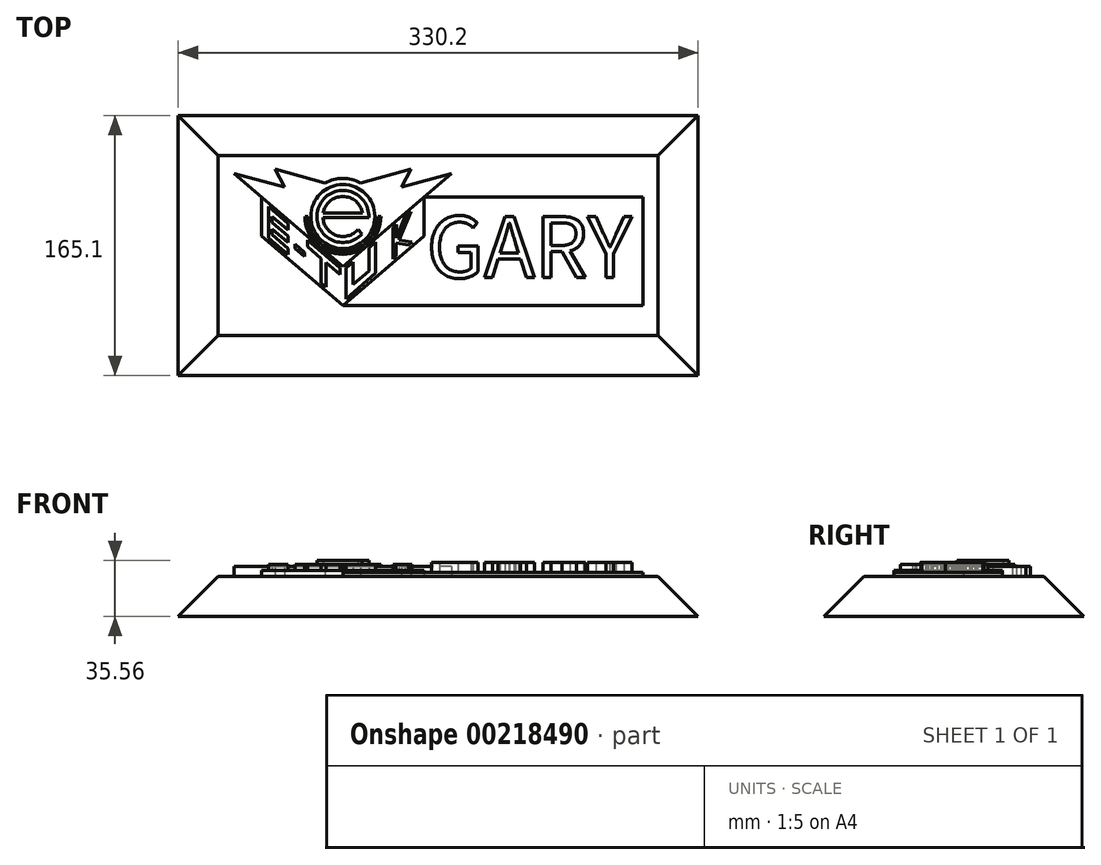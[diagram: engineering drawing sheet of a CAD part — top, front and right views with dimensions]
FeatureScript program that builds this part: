
annotation { "Feature Type Name" : "Feature", "Feature Type Description" : "" }
export const myFeature = defineFeature(function(context is Context, id is Id, definition is map)
    precondition{}
    {
        {
            var Q0;
            Q0=qCreatedBy(makeId("Top.planeOp"),FACE);
            var sketch = newSketch(context, id + "F0", { "sketchPlane" : qUnion([Q0])});
            skArc(sketch, "E0", {"start": v(12.53, 2.07) * mm, "mid": v(0, 12.7) * mm, "end": v(-12.53, 2.07) * mm});
            skArc(sketch, "E1", {"start": v(16.5, -0.78) * mm, "mid": v(-15.23, 6.37) * mm, "end": v(12.14, -11.18) * mm});
            skLineSegment(sketch, "E2", {"start": v(12.7, -0.78) * mm, "end": v(-12.68, -0.78) * mm});
            skLineSegment(sketch, "E3", {"start": v(-12.68, -0.78) * mm, "end": v(16.5, -0.78) * mm});
            skLineSegment(sketch, "E4", {"start": v(9.59, -8.33) * mm, "end": v(12.14, -11.18) * mm});
            skArc(sketch, "E5.trimOffspring", {"start": v(-12.68, -0.78) * mm, "mid": v(-4.08, -12.03) * mm, "end": v(9.59, -8.33) * mm});
            skLineSegment(sketch, "E6", {"start": v(-12.53, 2.07) * mm, "end": v(12.53, 2.07) * mm});
            skSolve(sketch);
        }
        {
            var Q0;
            Q0=makeQuery(id+"F0.imprint","IMPRINT",FACE,{"disambiguationData":[TD([[makeQuery(id+"F0.imprint","IMPRINT",EDGE,{"derivedFrom":sQuery(id+"F0.wireOp",EDGE,"E0")}),-1.0]])]});
            extrude(context, id + "F1", {"entities" : qUnion([Q0]), "depth" : 10.16 * mm});
        }
        {
            var Q0;
            Q0=qCreatedBy(makeId("Top.planeOp"),FACE);
            var sketch = newSketch(context, id + "F2", { "sketchPlane" : qUnion([Q0])});
            skCircle(sketch, "E7", {"center": v(0, 0) * mm, "radius": 20.32 * mm});
            skSolve(sketch);
        }
        {
            var Q0;
            Q0=qSketchRegion(id+"F2",true);
            extrude(context, id + "F3", {"entities" : qUnion([Q0]), "operationType" : NewBodyOperationType.ADD, "depth" : 7.62 * mm});
        }
        {
            var Q0;
            Q0=qCreatedBy(makeId("Top.planeOp"),FACE);
            var sketch = newSketch(context, id + "F4", { "sketchPlane" : qUnion([Q0])});
            skLineSegment(sketch, "E8", {"start": v(-69.02, 27.27) * mm, "end": v(-37.13, 18.72) * mm});
            skLineSegment(sketch, "E9", {"start": v(-37.13, 18.72) * mm, "end": v(-43.14, 30.14) * mm});
            skLineSegment(sketch, "E10", {"start": v(-43.14, 30.14) * mm, "end": v(-11.32, 21.31) * mm});
            skLineSegment(sketch, "E11", {"start": v(-69.02, 27.27) * mm, "end": v(0, -31.75) * mm});
            skLineSegment(sketch, "E12.MirrorCS", {"start": v(43.14, 30.14) * mm, "end": v(11.32, 21.31) * mm});
            skLineSegment(sketch, "E13.MirrorCS", {"start": v(69.02, 27.27) * mm, "end": v(0, -31.75) * mm});
            skLineSegment(sketch, "E14.MirrorCS", {"start": v(69.02, 27.27) * mm, "end": v(37.13, 18.72) * mm});
            skLineSegment(sketch, "E15.MirrorCS", {"start": v(37.13, 18.72) * mm, "end": v(43.14, 30.14) * mm});
            skArc(sketch, "E16.trimOffspring", {"start": v(11.32, 21.31) * mm, "mid": v(0, 24.13) * mm, "end": v(-11.32, 21.31) * mm});
            skSolve(sketch);
        }
        {
            var Q0;
            Q0=qSketchRegion(id+"F4",true);
            var Q1;
            Q1=makeQuery(id+"F2.imprint","IMPRINT",FACE,{"disambiguationData":[TD([[makeQuery(id+"F2.imprint","IMPRINT",EDGE,{"derivedFrom":sQuery(id+"F2.wireOp",EDGE,"E7")}),1.0]])]});
            extrude(context, id + "F5", {"entities" : qUnion([Q0, Q1]), "operationType" : NewBodyOperationType.ADD, "depth" : 6.35 * mm});
        }
        {
            var Q0;
            Q0=qCreatedBy(makeId("Top.planeOp"),FACE);
            var sketch = newSketch(context, id + "F6", { "sketchPlane" : qUnion([Q0])});
            skLineSegment(sketch, "E17", {"start": v(-51.6, -12.38) * mm, "end": v(0, -56.51) * mm});
            skLineSegment(sketch, "E18", {"start": v(0, -56.51) * mm, "end": v(51.6, -12.38) * mm});
            skLineSegment(sketch, "E19", {"start": v(-51.6, 12.38) * mm, "end": v(-51.6, -12.38) * mm});
            skLineSegment(sketch, "E20", {"start": v(51.6, 12.38) * mm, "end": v(51.6, -12.38) * mm});
            skLineSegment(sketch, "E21", {"start": v(-51.6, 12.38) * mm, "end": v(0, -31.75) * mm});
            skLineSegment(sketch, "E22", {"start": v(0, -31.75) * mm, "end": v(51.6, 12.38) * mm});
            skSolve(sketch);
        }
        {
            var Q0;
            Q0=qSketchRegion(id+"F6",true);
            extrude(context, id + "F7", {"entities" : qUnion([Q0]), "operationType" : NewBodyOperationType.ADD, "depth" : 3.8 * mm});
        }
        {
            var Q0;
            Q0=makeQuery(id+"F7.opExtrude","CAP_FACE",FACE,{"disambiguationData":[OSD([sQuery(id+"F6.wireOp",EDGE,"E17"),sQuery(id+"F6.wireOp",EDGE,"E18"),sQuery(id+"F6.wireOp",EDGE,"E19"),sQuery(id+"F6.wireOp",EDGE,"E20"),sQuery(id+"F6.wireOp",EDGE,"E21"),sQuery(id+"F6.wireOp",EDGE,"E22")])],"isStart":false});
            var sketch = newSketch(context, id + "F8", { "sketchPlane" : qUnion([Q0])});
            skPoint(sketch, "E23.startSnap0", {"position": v(-51.6, 0) * mm});
            skLineSegment(sketch, "E24", {"start": v(-51.6, -9.87) * mm, "end": v(-51.6, 9.87) * mm, "construction": true});
            skLineSegment(sketch, "E25", {"start": v(-47.26, 6.16) * mm, "end": v(-34.74, -4.55) * mm});
            skLineSegment(sketch, "E26", {"start": v(-34.74, -4.55) * mm, "end": v(-34.74, -8.63) * mm});
            skLineSegment(sketch, "E27", {"start": v(-34.74, -8.63) * mm, "end": v(-44.83, 0) * mm});
            skLineSegment(sketch, "E28", {"start": v(-44.83, 0) * mm, "end": v(-44.83, -3.75) * mm});
            skLineSegment(sketch, "E29", {"start": v(-44.83, -3.75) * mm, "end": v(-34.74, -12.38) * mm});
            skLineSegment(sketch, "E30", {"start": v(-34.74, -12.38) * mm, "end": v(-34.74, -16.46) * mm});
            skLineSegment(sketch, "E31", {"start": v(-34.74, -16.46) * mm, "end": v(-44.83, -7.83) * mm});
            skLineSegment(sketch, "E32", {"start": v(-44.83, -7.83) * mm, "end": v(-44.83, -11.58) * mm});
            skLineSegment(sketch, "E33", {"start": v(-44.83, -11.58) * mm, "end": v(-34.74, -20.21) * mm});
            skLineSegment(sketch, "E34", {"start": v(-34.74, -20.21) * mm, "end": v(-34.74, -24.3) * mm});
            skLineSegment(sketch, "E35", {"start": v(-34.74, -24.3) * mm, "end": v(-47.26, -13.59) * mm});
            skLineSegment(sketch, "E36", {"start": v(-47.26, 6.16) * mm, "end": v(-47.26, -13.59) * mm});
            skLineSegment(sketch, "E37", {"start": v(-30.38, -20.21) * mm, "end": v(-30.38, -17.65) * mm});
            skLineSegment(sketch, "E38", {"start": v(-30.38, -17.65) * mm, "end": v(-24.17, -22.96) * mm});
            skLineSegment(sketch, "E39", {"start": v(-24.17, -22.96) * mm, "end": v(-24.17, -25.53) * mm});
            skLineSegment(sketch, "E40", {"start": v(-24.17, -25.53) * mm, "end": v(-30.38, -20.21) * mm});
            skLineSegment(sketch, "E41", {"start": v(-22.38, -15.12) * mm, "end": v(-1.9, -32.63) * mm});
            skLineSegment(sketch, "E42", {"start": v(-1.9, -32.63) * mm, "end": v(-1.9, -36.71) * mm});
            skLineSegment(sketch, "E43", {"start": v(-1.9, -36.71) * mm, "end": v(-10.6, -29.28) * mm});
            skLineSegment(sketch, "E44", {"start": v(-10.6, -29.28) * mm, "end": v(-10.6, -44.95) * mm});
            skLineSegment(sketch, "E45", {"start": v(-10.6, -44.95) * mm, "end": v(-13.7, -42.3) * mm});
            skLineSegment(sketch, "E46", {"start": v(-13.7, -42.3) * mm, "end": v(-13.7, -26.63) * mm});
            skLineSegment(sketch, "E47", {"start": v(-13.7, -26.63) * mm, "end": v(-22.38, -19.2) * mm});
            skLineSegment(sketch, "E48", {"start": v(-22.38, -19.2) * mm, "end": v(-22.38, -15.12) * mm});
            skLineSegment(sketch, "E49", {"start": v(1.9, -32.62) * mm, "end": v(6.3, -28.86) * mm});
            skLineSegment(sketch, "E50", {"start": v(6.3, -28.86) * mm, "end": v(6.3, -43.26) * mm});
            skLineSegment(sketch, "E51", {"start": v(6.3, -43.26) * mm, "end": v(16.5, -34.54) * mm});
            skLineSegment(sketch, "E52", {"start": v(16.5, -34.54) * mm, "end": v(16.5, -20.14) * mm});
            skLineSegment(sketch, "E53", {"start": v(16.5, -20.14) * mm, "end": v(20.85, -16.3) * mm});
            skLineSegment(sketch, "E54", {"start": v(20.85, -16.3) * mm, "end": v(20.85, -36.06) * mm});
            skLineSegment(sketch, "E55", {"start": v(20.85, -36.06) * mm, "end": v(1.9, -52.37) * mm});
            skLineSegment(sketch, "E56", {"start": v(1.9, -52.37) * mm, "end": v(1.9, -32.62) * mm});
            skLineSegment(sketch, "E57", {"start": v(31.73, -7.12) * mm, "end": v(31.73, -27.15) * mm});
            skLineSegment(sketch, "E58", {"start": v(31.73, -27.15) * mm, "end": v(33.91, -25.22) * mm});
            skLineSegment(sketch, "E59", {"start": v(33.91, -25.22) * mm, "end": v(33.91, -16.82) * mm});
            skLineSegment(sketch, "E60", {"start": v(33.94, -13.64) * mm, "end": v(33.94, -5.23) * mm});
            skLineSegment(sketch, "E61", {"start": v(33.94, -5.23) * mm, "end": v(31.73, -7.12) * mm});
            skLineSegment(sketch, "E62", {"start": v(41.79, -18.27) * mm, "end": v(44, -16.38) * mm});
            skLineSegment(sketch, "E63", {"start": v(33.94, -13.64) * mm, "end": v(39.5, 0) * mm});
            skLineSegment(sketch, "E64", {"start": v(33.91, -16.82) * mm, "end": v(41.79, -18.27) * mm});
            skLineSegment(sketch, "E65", {"start": v(44, -16.38) * mm, "end": v(35.85, -14.87) * mm});
            skLineSegment(sketch, "E66", {"start": v(35.85, -14.87) * mm, "end": v(43.2, 3.16) * mm});
            skLineSegment(sketch, "E67", {"start": v(39.5, 0) * mm, "end": v(43.2, 3.16) * mm});
            skSolve(sketch);
        }
        {
            var Q0;
            Q0=qSketchRegion(id+"F8",true);
            extrude(context, id + "F9", {"entities" : qUnion([Q0]), "operationType" : NewBodyOperationType.ADD, "depth" : 3.8 * mm});
        }
        {
            var Q0;
            Q0=makeQuery(id+"F5.boolean.opBoolean","MERGE",FACE,{"derivedFrom":[makeQuery(id+"F5.opExtrude","CAP_FACE",FACE,{"disambiguationData":[OSD([sQuery(id+"F2.wireOp",EDGE,"E7")])],"isStart":false}),makeQuery(id+"F5.opExtrude","CAP_FACE",FACE,{"disambiguationData":[OSD([sQuery(id+"F4.wireOp",EDGE,"E8"),sQuery(id+"F4.wireOp",EDGE,"E9"),sQuery(id+"F4.wireOp",EDGE,"E10"),sQuery(id+"F4.wireOp",EDGE,"E11"),sQuery(id+"F4.wireOp",EDGE,"E13.MirrorCS"),sQuery(id+"F4.wireOp",EDGE,"E14.MirrorCS"),sQuery(id+"F4.wireOp",EDGE,"E12.MirrorCS"),sQuery(id+"F4.wireOp",EDGE,"E15.MirrorCS"),sQuery(id+"F4.wireOp",EDGE,"E16.trimOffspring")])],"isStart":false})]});
            var sketch = newSketch(context, id + "F10", { "sketchPlane" : qUnion([Q0])});
            skArc(sketch, "E68", {"start": v(-24.13, 0) * mm, "mid": v(0, -24.13) * mm, "end": v(24.13, 0) * mm});
            skArc(sketch, "E69", {"start": v(-22.23, 0) * mm, "mid": v(0, -22.23) * mm, "end": v(22.23, 0) * mm});
            skLineSegment(sketch, "E70", {"start": v(-24.13, 0) * mm, "end": v(-22.23, 0) * mm});
            skLineSegment(sketch, "E71", {"start": v(24.13, 0) * mm, "end": v(22.23, 0) * mm});
            skSolve(sketch);
        }
        {
            var Q0;
            Q0=qSketchRegion(id+"F10",true);
            extrude(context, id + "F11", {"entities" : qUnion([Q0]), "operationType" : NewBodyOperationType.ADD, "depth" : 1.27 * mm});
        }
        {
            var Q0;
            {var subQ0=sQuery(id+"F2.wireOp",EDGE,"E7");Q0=makeQuery(id+"F7.boolean.opBoolean","MERGE",FACE,{"derivedFrom":[makeQuery(id+"F5.boolean.opBoolean","MERGE",FACE,{"derivedFrom":[makeQuery(id+"F3.boolean.opBoolean","MERGE",FACE,{"derivedFrom":[makeQuery(id+"F1.opExtrude","CAP_FACE",FACE,{"disambiguationData":[OSD([sQuery(id+"F0.wireOp",EDGE,"E0"),sQuery(id+"F0.wireOp",EDGE,"E1"),sQuery(id+"F0.wireOp",EDGE,"E3"),sQuery(id+"F0.wireOp",EDGE,"E4"),sQuery(id+"F0.wireOp",EDGE,"E5.trimOffspring"),sQuery(id+"F0.wireOp",EDGE,"E6")])],"isStart":true}),makeQuery(id+"F3.opExtrude","CAP_FACE",FACE,{"disambiguationData":[OSD([subQ0])],"isStart":true})]}),makeQuery(id+"F5.opExtrude","CAP_FACE",FACE,{"disambiguationData":[OSD([subQ0])],"isStart":true}),makeQuery(id+"F5.opExtrude","CAP_FACE",FACE,{"disambiguationData":[OSD([sQuery(id+"F4.wireOp",EDGE,"E8"),sQuery(id+"F4.wireOp",EDGE,"E9"),sQuery(id+"F4.wireOp",EDGE,"E10"),sQuery(id+"F4.wireOp",EDGE,"E11"),sQuery(id+"F4.wireOp",EDGE,"E13.MirrorCS"),sQuery(id+"F4.wireOp",EDGE,"E14.MirrorCS"),sQuery(id+"F4.wireOp",EDGE,"E12.MirrorCS"),sQuery(id+"F4.wireOp",EDGE,"E15.MirrorCS"),sQuery(id+"F4.wireOp",EDGE,"E16.trimOffspring")])],"isStart":true})]}),makeQuery(id+"F7.opExtrude","CAP_FACE",FACE,{"disambiguationData":[OSD([sQuery(id+"F6.wireOp",EDGE,"E17"),sQuery(id+"F6.wireOp",EDGE,"E18"),sQuery(id+"F6.wireOp",EDGE,"E19"),sQuery(id+"F6.wireOp",EDGE,"E20"),sQuery(id+"F6.wireOp",EDGE,"E21"),sQuery(id+"F6.wireOp",EDGE,"E22")])],"isStart":true})]});}
            var sketch = newSketch(context, id + "F12", { "sketchPlane" : qUnion([Q0])});
            skLineSegment(sketch, "E72.bottom", {"start": v(0, 56.51) * mm, "end": v(190.5, 56.51) * mm});
            skLineSegment(sketch, "E72.right", {"start": v(190.5, 56.51) * mm, "end": v(190.5, -12.38) * mm});
            skLineSegment(sketch, "E73", {"start": v(51.6, -12.38) * mm, "end": v(190.5, -12.38) * mm});
            skLineSegment(sketch, "E74", {"start": v(0, 56.51) * mm, "end": v(51.6, 12.38) * mm});
            skLineSegment(sketch, "E75", {"start": v(51.6, 12.38) * mm, "end": v(51.6, -12.38) * mm});
            skSolve(sketch);
        }
        {
            var Q0;
            Q0=qSketchRegion(id+"F12",true);
            extrude(context, id + "F13", {"entities" : qUnion([Q0]), "operationType" : NewBodyOperationType.ADD, "oppositeDirection" : true, "depth" : 2.54 * mm});
        }
        {
            var Q0;
            Q0=makeQuery(id+"F13.opExtrude","CAP_FACE",FACE,{"disambiguationData":[OSD([sQuery(id+"F12.wireOp",EDGE,"E72.bottom"),sQuery(id+"F12.wireOp",EDGE,"E72.right"),sQuery(id+"F12.wireOp",EDGE,"E73"),sQuery(id+"F12.wireOp",EDGE,"E74"),sQuery(id+"F12.wireOp",EDGE,"E75")])],"isStart":false});
            var sketch = newSketch(context, id + "F14", { "sketchPlane" : qUnion([Q0])});
            skText(sketch, "E76", { "text": "GARY", "fontName": "NotoSansCJKkr-Regular.otf"});
            const initialGuessF14  = {"E76": [0.05333, -0.03885, 1, 0, 0.0381]};
            skSetInitialGuess(sketch, initialGuessF14);
            skSolve(sketch);
        }
        {
            var Q0;
            Q0=qSketchRegion(id+"F14",true);
            extrude(context, id + "F15", {"entities" : qUnion([Q0]), "operationType" : NewBodyOperationType.ADD, "depth" : 6.35 * mm});
        }
        {
            var Q0;
            Q0=makeQuery(id+"F13.opExtrude","CAP_FACE",FACE,{"disambiguationData":[OSD([sQuery(id+"F12.wireOp",EDGE,"E72.bottom"),sQuery(id+"F12.wireOp",EDGE,"E72.right"),sQuery(id+"F12.wireOp",EDGE,"E73"),sQuery(id+"F12.wireOp",EDGE,"E74"),sQuery(id+"F12.wireOp",EDGE,"E75")])],"isStart":true});
            var sketch = newSketch(context, id + "F16", { "sketchPlane" : qUnion([Q0])});
            skLineSegment(sketch, "E77.bottom", {"start": v(-79.18, -38.74) * mm, "end": v(200.22, -38.74) * mm});
            skLineSegment(sketch, "E77.top", {"start": v(-79.18, 75.56) * mm, "end": v(200.22, 75.56) * mm});
            skLineSegment(sketch, "E77.left", {"start": v(-79.18, -38.74) * mm, "end": v(-79.18, 75.56) * mm});
            skLineSegment(sketch, "E77.right", {"start": v(200.22, -38.74) * mm, "end": v(200.22, 75.56) * mm});
            skSolve(sketch);
        }
        {
            var Q0;
            Q0=qSketchRegion(id+"F16",true);
            extrude(context, id + "F17", {"entities" : qUnion([Q0]), "operationType" : NewBodyOperationType.ADD, "depth" : 25.4 * mm, "hasDraft" : true, "draftAngle" : 45 * degree});
        }
    });
